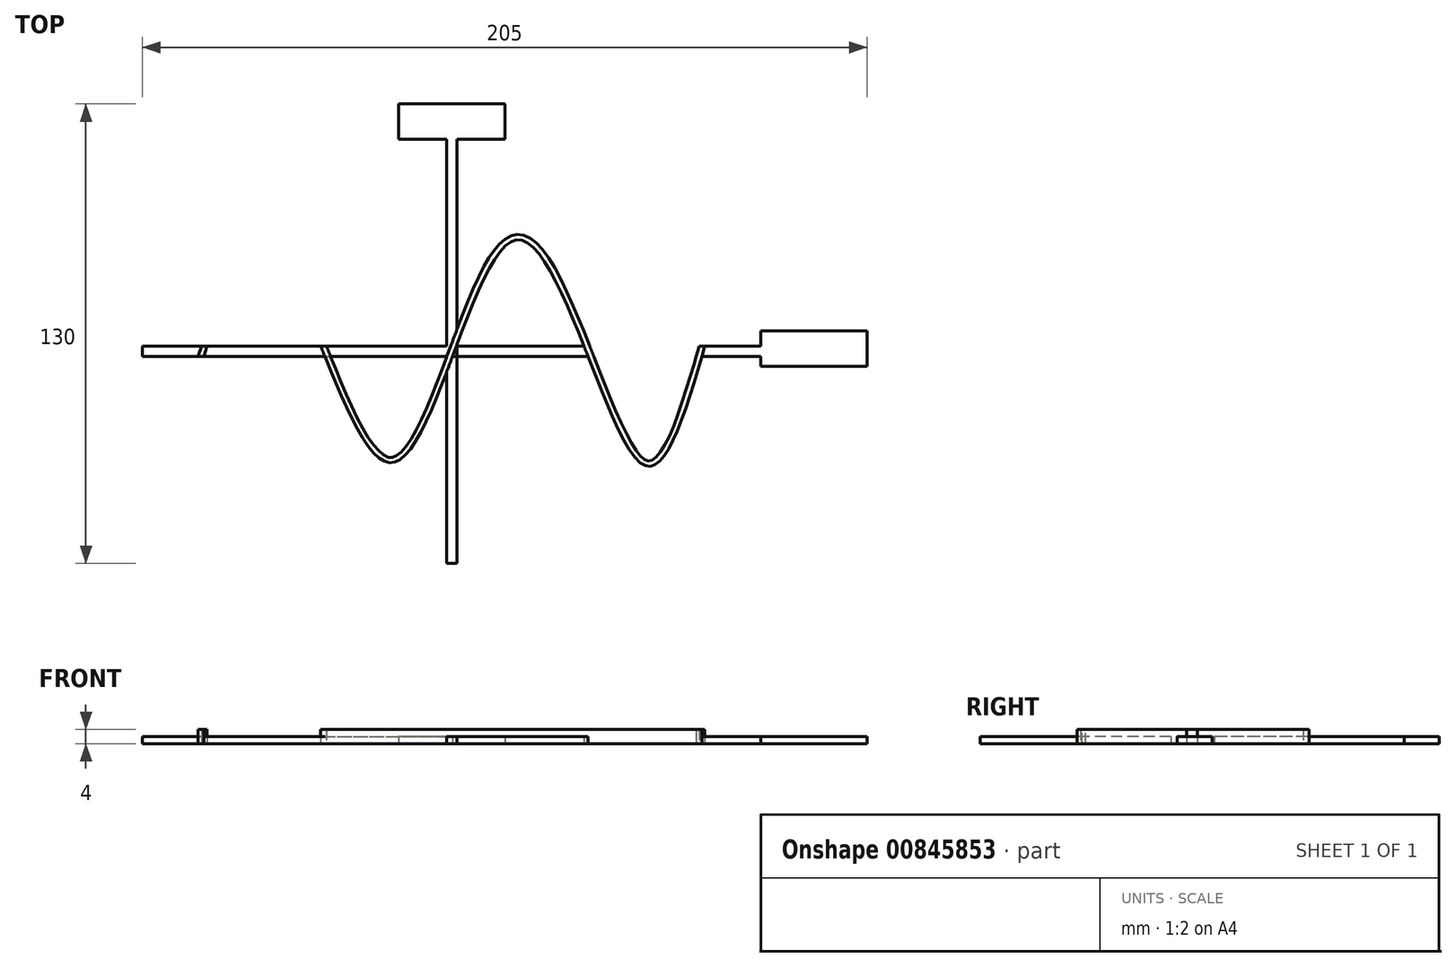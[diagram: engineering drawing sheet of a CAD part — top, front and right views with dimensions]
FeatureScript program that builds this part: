
annotation { "Feature Type Name" : "Feature", "Feature Type Description" : "" }
export const myFeature = defineFeature(function(context is Context, id is Id, definition is map)
    precondition{}
    {
        {
            var Q0;
            Q0=qCreatedBy(makeId("Top.planeOp"),FACE);
            var sketch = newSketch(context, id + "F0", { "sketchPlane" : qUnion([Q0])});
            skLineSegment(sketch, "E0.bottom", {"start": v(-87.5, 1.5) * mm, "end": v(87.5, 1.5) * mm});
            skLineSegment(sketch, "E0.top", {"start": v(-87.5, -1.5) * mm, "end": v(-71.78, -1.5) * mm});
            skLineSegment(sketch, "E0.left", {"start": v(-87.5, 1.5) * mm, "end": v(-87.5, -1.5) * mm});
            skLineSegment(sketch, "E0.right", {"start": v(87.5, 1.5) * mm, "end": v(87.5, -1.5) * mm});
            skLineSegment(sketch, "E1.bottom", {"start": v(-1.5, 60) * mm, "end": v(1.5, 60) * mm});
            skLineSegment(sketch, "E1.top", {"start": v(-1.5, -60) * mm, "end": v(1.5, -60) * mm});
            skLineSegment(sketch, "E1.left", {"start": v(-1.5, 60) * mm, "end": v(-1.5, -60) * mm});
            skLineSegment(sketch, "E1.right", {"start": v(1.5, 60) * mm, "end": v(1.5, -60) * mm});
            skPoint(sketch, "E1.middle", {"position": v(0, 0) * mm});
            skLineSegment(sketch, "E2.bottom", {"start": v(15, 60) * mm, "end": v(-15, 60) * mm});
            skLineSegment(sketch, "E2.top", {"start": v(15, 70) * mm, "end": v(-15, 70) * mm});
            skLineSegment(sketch, "E2.left", {"start": v(15, 60) * mm, "end": v(15, 70) * mm});
            skLineSegment(sketch, "E2.right", {"start": v(-15, 60) * mm, "end": v(-15, 70) * mm});
            skPoint(sketch, "E2.middle", {"position": v(0, 65) * mm});
            skPoint(sketch, "E3", {"position": v(0, 60) * mm});
            skLineSegment(sketch, "E4.bottom", {"start": v(101, -4.26) * mm, "end": v(104, -4.26) * mm});
            skLineSegment(sketch, "E5.bottom", {"start": v(117.5, -4.26) * mm, "end": v(87.5, -4.26) * mm});
            skLineSegment(sketch, "E5.top", {"start": v(117.5, 5.74) * mm, "end": v(87.5, 5.74) * mm});
            skLineSegment(sketch, "E5.left", {"start": v(117.5, -4.26) * mm, "end": v(117.5, 5.74) * mm});
            skLineSegment(sketch, "E5.right", {"start": v(87.5, -4.26) * mm, "end": v(87.5, 5.74) * mm});
            skPoint(sketch, "E5.middle", {"position": v(102.5, 0.74) * mm});
            skPoint(sketch, "E6", {"position": v(102.5, -4.26) * mm});
            skPoint(sketch, "E7", {"position": v(87.5, 0) * mm});
            skPoint(sketch, "E8", {"position": v(0, 1.5) * mm});
            skLineSegment(sketch, "E9", {"start": v(-90, 31.5) * mm, "end": v(86.69, 31.5) * mm, "construction": true});
            skLineSegment(sketch, "E10", {"start": v(-87.09, -31.5) * mm, "end": v(87.56, -31.5) * mm, "construction": true});
            skPoint(sketch, "E11", {"position": v(-70, 31.5) * mm});
            skPoint(sketch, "E12", {"position": v(0, 31.5) * mm});
            skPoint(sketch, "E13", {"position": v(70, 31.5) * mm});
            skPoint(sketch, "E14", {"position": v(-35, -31.5) * mm});
            skPoint(sketch, "E15", {"position": v(35, -31.5) * mm});
            skPoint(sketch, "E16", {"position": v(-70, -31.5) * mm});
            skPoint(sketch, "E17", {"position": v(0.24, -31.5) * mm});
            skPoint(sketch, "E18", {"position": v(70, -31.5) * mm});
            skPoint(sketch, "E19", {"position": v(-35, 31.5) * mm});
            skPoint(sketch, "E20", {"position": v(35, 31.5) * mm});
            skPoint(sketch, "E21", {"position": v(-17.5, -31.5) * mm});
            skPoint(sketch, "E22", {"position": v(17.5, -31.5) * mm});
            skPoint(sketch, "E23", {"position": v(52.5, -31.5) * mm});
            skPoint(sketch, "E24", {"position": v(17.5, 31.5) * mm});
            skPoint(sketch, "E25", {"position": v(52.5, 31.5) * mm});
            skPoint(sketch, "E26", {"position": v(-52.5, 31.5) * mm});
            skPoint(sketch, "E27", {"position": v(-52.5, -31.5) * mm});
            skPoint(sketch, "E28", {"position": v(-17.5, 31.5) * mm});
            skFitSpline(sketch, "E29", {"points": [v(-69.25, 1.5) * mm, v(-51.75, 31.5) * mm, v(-16.75, -31.5) * mm, v(18.25, 31.5) * mm, v(53.25, -31.5) * mm, v(70.75, -1.5) * mm], "startDerivative": vector(100.86, 337.44) * mm, "endDerivative": vector(100.86, 337.44) * mm});
            skFitSpline(sketch, "E30.0", {"points": [v(-70.69, 1.93) * mm, v(-70.16, 3.69) * mm, v(-69.1, 7.2) * mm, v(-67.52, 12.36) * mm, v(-65.9, 17.26) * mm, v(-64.26, 21.78) * mm, v(-62.55, 25.79) * mm, v(-61.07, 28.6) * mm, v(-59.82, 30.5) * mm, v(-58.83, 31.73) * mm, v(-57.76, 32.75) * mm, v(-56.58, 33.53) * mm, v(-55.26, 34.02) * mm, v(-53.82, 34.1) * mm, v(-52.4, 33.72) * mm, v(-51.1, 32.96) * mm, v(-49.89, 31.87) * mm, v(-48.74, 30.5) * mm, v(-47.6, 28.87) * mm, v(-46.1, 26.37) * mm, v(-44.21, 22.67) * mm, v(-41.9, 17.49) * mm, v(-39.54, 11.77) * mm, v(-37.13, 5.7) * mm, v(-34.69, -0.51) * mm, v(-32.22, -6.66) * mm, v(-29.73, -12.53) * mm, v(-27.24, -17.91) * mm, v(-24.76, -22.6) * mm, v(-22.72, -25.73) * mm, v(-21.15, -27.65) * mm, v(-20.02, -28.77) * mm, v(-18.97, -29.54) * mm, v(-18.04, -29.95) * mm, v(-17.38, -30.05) * mm, v(-16.89, -30.01) * mm, v(-16.37, -29.89) * mm, v(-15.63, -29.54) * mm, v(-14.61, -28.75) * mm, v(-13.52, -27.58) * mm, v(-12.01, -25.58) * mm, v(-10.08, -22.31) * mm, v(-7.73, -17.43) * mm, v(-5.37, -11.84) * mm, v(-3.02, -5.78) * mm, v(-0.66, 0.52) * mm, v(1.71, 6.85) * mm, v(4.09, 12.96) * mm, v(6.49, 18.65) * mm, v(8.5, 22.86) * mm, v(10.16, 25.8) * mm, v(11.41, 27.78) * mm, v(12.7, 29.5) * mm, v(14.04, 30.93) * mm, v(15.47, 32.07) * mm, v(16.78, 32.71) * mm, v(17.9, 32.99) * mm, v(19.06, 33.08) * mm, v(20.48, 32.84) * mm, v(22.05, 32.1) * mm, v(23.5, 31.03) * mm, v(24.89, 29.65) * mm, v(26.68, 27.46) * mm, v(28.86, 24.1) * mm, v(31.43, 19.23) * mm, v(33.98, 13.73) * mm, v(36.5, 7.8) * mm, v(38.98, 1.61) * mm, v(41.42, -4.6) * mm, v(43.82, -10.65) * mm, v(46.16, -16.31) * mm, v(48.43, -21.39) * mm, v(50.25, -24.94) * mm, v(51.64, -27.25) * mm, v(52.64, -28.7) * mm, v(53.42, -29.62) * mm, v(54, -30.18) * mm, v(54.53, -30.6) * mm, v(55.1, -30.93) * mm, v(55.65, -31.06) * mm, v(56.13, -31.04) * mm, v(56.68, -30.85) * mm, v(57.35, -30.42) * mm, v(58.1, -29.71) * mm, v(58.88, -28.74) * mm, v(59.96, -27.12) * mm, v(61.33, -24.53) * mm, v(62.96, -20.7) * mm, v(64.57, -16.29) * mm, v(66.16, -11.46) * mm, v(67.74, -6.34) * mm, v(68.79, -2.83) * mm, v(69.31, -1.07) * mm]});
            skFitSpline(sketch, "E31", {"points": [v(-70.69, 1.93) * mm, v(-71.77, -1.5) * mm, v(-71.78, -1.5) * mm], "startDerivative": vector(-1.57, -5.39) * mm, "endDerivative": vector(-0.25, 0.12) * mm});
            skFitSpline(sketch, "E32.trimOffspring", {"points": [v(-70.69, 1.93) * mm, v(-71.77, -1.5) * mm, v(-71.78, -1.5) * mm], "startDerivative": vector(-1.57, -5.39) * mm, "endDerivative": vector(-0.25, 0.12) * mm});
            skLineSegment(sketch, "E33.trimOffspring", {"start": v(-71.77, -1.5) * mm, "end": v(87.5, -1.5) * mm});
            skLineSegment(sketch, "E34", {"start": v(69.18, -1.5) * mm, "end": v(70.01, 1.5) * mm});
            skLineSegment(sketch, "E35", {"start": v(70.75, -1.5) * mm, "end": v(71.57, 1.5) * mm});
            skLineSegment(sketch, "E36", {"start": v(-70.81, 1.5) * mm, "end": v(-71.77, -1.5) * mm});
            skLineSegment(sketch, "E37", {"start": v(-69.25, 1.5) * mm, "end": v(-70.2, -1.5) * mm});
            skSolve(sketch);
        }
        {
            var Q0;
            Q0=makeQuery(id+"F0.imprint","IMPRINT",FACE,{"disambiguationData":[TD([[makeQuery(id+"F0.imprint","IMPRINT",EDGE,{"derivedFrom":sQuery(id+"F0.wireOp",EDGE,"E0.top")}),1.0]])]});
            var Q1;
            {var subQ0=sQuery(id+"F0.wireOp",EDGE,"E30.0");var subQ1=sQuery(id+"F0.wireOp",EDGE,"E0.bottom");var subQ2=makeQuery(id+"F0.imprint","INTERSECT",VERTEX,{"disambiguationData":[OD(0.0)],"derivedFrom":[subQ1,subQ0]});Q1=makeQuery(id+"F0.imprint","IMPRINT",FACE,{"disambiguationData":[TD([[makeQuery(id+"F0.imprint","IMPRINT",EDGE,{"disambiguationData":[TD([[subQ2,-1.0]])],"derivedFrom":subQ1}),-1.0]])]});}
            var Q2;
            {var subQ5=sQuery(id+"F0.wireOp",EDGE,"E1.left");var subQ7=sQuery(id+"F0.wireOp",EDGE,"E0.bottom");var subQ8=makeQuery(id+"F0.imprint","INTERSECT",VERTEX,{"derivedFrom":[subQ7,subQ5]});Q2=makeQuery(id+"F0.imprint","IMPRINT",FACE,{"disambiguationData":[TD([[makeQuery(id+"F0.imprint","IMPRINT",EDGE,{"disambiguationData":[TD([[subQ8,-1.0]])],"derivedFrom":subQ7}),1.0]])]});}
            var Q3;
            {var subQ7=sQuery(id+"F0.wireOp",EDGE,"E1.top");Q3=makeQuery(id+"F0.imprint","IMPRINT",FACE,{"disambiguationData":[TD([[makeQuery(id+"F0.imprint","IMPRINT",EDGE,{"derivedFrom":subQ7}),1.0]])]});}
            var Q4;
            {var subQ0=sQuery(id+"F0.wireOp",EDGE,"E1.right");var subQ1=sQuery(id+"F0.wireOp",EDGE,"E0.bottom");var subQ2=makeQuery(id+"F0.imprint","INTERSECT",VERTEX,{"derivedFrom":[subQ1,subQ0]});Q4=makeQuery(id+"F0.imprint","IMPRINT",FACE,{"disambiguationData":[TD([[makeQuery(id+"F0.imprint","IMPRINT",EDGE,{"disambiguationData":[TD([[subQ2,-1.0]])],"derivedFrom":subQ1}),-1.0]])]});}
            var Q5;
            {var subQ1=sQuery(id+"F0.wireOp",EDGE,"E0.bottom");var subQ6=sQuery(id+"F0.wireOp",EDGE,"E5.right");var subQ7=makeQuery(id+"F0.imprint","INTERSECT",VERTEX,{"derivedFrom":[subQ1,subQ6]});Q5=makeQuery(id+"F0.imprint","IMPRINT",FACE,{"disambiguationData":[TD([[makeQuery(id+"F0.imprint","IMPRINT",EDGE,{"disambiguationData":[TD([[subQ7,1.0]])],"derivedFrom":subQ1}),-1.0]])]});}
            var Q6;
            {var subQ5=sQuery(id+"F0.wireOp",EDGE,"E5.top");Q6=makeQuery(id+"F0.imprint","IMPRINT",FACE,{"disambiguationData":[TD([[makeQuery(id+"F0.imprint","IMPRINT",EDGE,{"derivedFrom":subQ5}),1.0]])]});}
            var Q7;
            Q7=makeQuery(id+"F0.imprint","IMPRINT",FACE,{"disambiguationData":[TD([[makeQuery(id+"F0.imprint","IMPRINT",EDGE,{"derivedFrom":sQuery(id+"F0.wireOp",EDGE,"E2.top")}),1.0]])]});
            var Q8;
            {var subQ0=sQuery(id+"F0.wireOp",EDGE,"E37");Q8=makeQuery(id+"F0.imprint","IMPRINT",FACE,{"disambiguationData":[TD([[makeQuery(id+"F0.imprint","IMPRINT",EDGE,{"derivedFrom":subQ0}),1.0]])]});}
            var Q9;
            {var subQ0=sQuery(id+"F0.wireOp",EDGE,"E34");Q9=makeQuery(id+"F0.imprint","IMPRINT",FACE,{"disambiguationData":[TD([[makeQuery(id+"F0.imprint","IMPRINT",EDGE,{"derivedFrom":subQ0}),1.0]])]});}
            var Q10;
            {var subQ0=sQuery(id+"F0.wireOp",EDGE,"E29");var subQ1=sQuery(id+"F0.wireOp",EDGE,"E0.bottom");var subQ2=makeQuery(id+"F0.imprint","INTERSECT",VERTEX,{"disambiguationData":[OD(1.0)],"derivedFrom":[subQ1,subQ0]});Q10=makeQuery(id+"F0.imprint","IMPRINT",FACE,{"disambiguationData":[TD([[makeQuery(id+"F0.imprint","IMPRINT",EDGE,{"disambiguationData":[TD([[subQ2,-1.0]])],"derivedFrom":subQ1}),-1.0]])]});}
            var Q11;
            {var subQ0=sQuery(id+"F0.wireOp",EDGE,"E1.left");var subQ1=sQuery(id+"F0.wireOp",EDGE,"E0.bottom");var subQ2=makeQuery(id+"F0.imprint","INTERSECT",VERTEX,{"derivedFrom":[subQ1,subQ0]});Q11=makeQuery(id+"F0.imprint","IMPRINT",FACE,{"disambiguationData":[TD([[makeQuery(id+"F0.imprint","IMPRINT",EDGE,{"disambiguationData":[TD([[subQ2,-1.0]])],"derivedFrom":subQ1}),-1.0]])]});}
            extrude(context, id + "F1", {"entities" : qUnion([Q0, Q1, Q2, Q3, Q4, Q5, Q6, Q7, Q8, Q9, Q10, Q11]), "depth" : 2 * mm, "offsetDistance" : 25 * mm});
        }
        {
            var Q0;
            {var subQ2=sQuery(id+"F0.wireOp",EDGE,"E36");Q0=makeQuery(id+"F0.imprint","IMPRINT",FACE,{"disambiguationData":[TD([[makeQuery(id+"F0.imprint","IMPRINT",EDGE,{"derivedFrom":subQ2}),1.0]])]});}
            var Q1;
            {var subQ0=sQuery(id+"F0.wireOp",EDGE,"E31");Q1=makeQuery(id+"F0.imprint","IMPRINT",FACE,{"disambiguationData":[TD([[makeQuery(id+"F0.imprint","IMPRINT",EDGE,{"derivedFrom":subQ0}),1.0]])]});}
            var Q2;
            {var subQ0=sQuery(id+"F0.wireOp",EDGE,"E30.0");var subQ1=sQuery(id+"F0.wireOp",EDGE,"E0.bottom");var subQ2=makeQuery(id+"F0.imprint","INTERSECT",VERTEX,{"disambiguationData":[OD(0.0)],"derivedFrom":[subQ1,subQ0]});Q2=makeQuery(id+"F0.imprint","IMPRINT",FACE,{"disambiguationData":[TD([[makeQuery(id+"F0.imprint","IMPRINT",EDGE,{"disambiguationData":[TD([[subQ2,1.0]])],"derivedFrom":subQ1}),-1.0]])]});}
            var Q3;
            {var subQ0=sQuery(id+"F0.wireOp",EDGE,"E29");var subQ1=sQuery(id+"F0.wireOp",EDGE,"E1.left");var subQ2=makeQuery(id+"F0.imprint","INTERSECT",VERTEX,{"derivedFrom":[subQ1,subQ0]});Q3=makeQuery(id+"F0.imprint","IMPRINT",FACE,{"disambiguationData":[TD([[makeQuery(id+"F0.imprint","IMPRINT",EDGE,{"disambiguationData":[TD([[subQ2,1.0]])],"derivedFrom":subQ1}),-1.0]])]});}
            var Q4;
            {var subQ0=sQuery(id+"F0.wireOp",EDGE,"E29");var subQ1=sQuery(id+"F0.wireOp",EDGE,"E1.left");var subQ2=makeQuery(id+"F0.imprint","INTERSECT",VERTEX,{"derivedFrom":[subQ1,subQ0]});Q4=makeQuery(id+"F0.imprint","IMPRINT",FACE,{"disambiguationData":[TD([[makeQuery(id+"F0.imprint","IMPRINT",EDGE,{"disambiguationData":[TD([[subQ2,1.0]])],"derivedFrom":subQ1}),1.0]])]});}
            var Q5;
            {var subQ0=sQuery(id+"F0.wireOp",EDGE,"E30.0");var subQ1=sQuery(id+"F0.wireOp",EDGE,"E0.bottom");var subQ2=makeQuery(id+"F0.imprint","INTERSECT",VERTEX,{"disambiguationData":[OD(2.0)],"derivedFrom":[subQ1,subQ0]});Q5=makeQuery(id+"F0.imprint","IMPRINT",FACE,{"disambiguationData":[TD([[makeQuery(id+"F0.imprint","IMPRINT",EDGE,{"disambiguationData":[TD([[subQ2,-1.0]])],"derivedFrom":subQ1}),-1.0]])]});}
            var Q6;
            {var subQ0=sQuery(id+"F0.wireOp",EDGE,"E30.0");var subQ1=sQuery(id+"F0.wireOp",EDGE,"E0.bottom");var subQ2=makeQuery(id+"F0.imprint","INTERSECT",VERTEX,{"disambiguationData":[OD(1.0)],"derivedFrom":[subQ1,subQ0]});Q6=makeQuery(id+"F0.imprint","IMPRINT",FACE,{"disambiguationData":[TD([[makeQuery(id+"F0.imprint","IMPRINT",EDGE,{"disambiguationData":[TD([[subQ2,1.0]])],"derivedFrom":subQ1}),1.0]])]});}
            var Q7;
            {var subQ0=sQuery(id+"F0.wireOp",EDGE,"E30.0");var subQ1=sQuery(id+"F0.wireOp",EDGE,"E0.bottom");var subQ2=makeQuery(id+"F0.imprint","INTERSECT",VERTEX,{"disambiguationData":[OD(2.0)],"derivedFrom":[subQ1,subQ0]});Q7=makeQuery(id+"F0.imprint","IMPRINT",FACE,{"disambiguationData":[TD([[makeQuery(id+"F0.imprint","IMPRINT",EDGE,{"disambiguationData":[TD([[subQ2,-1.0]])],"derivedFrom":subQ1}),1.0]])]});}
            var Q8;
            {var subQ0=sQuery(id+"F0.wireOp",EDGE,"E30.0");var subQ1=sQuery(id+"F0.wireOp",EDGE,"E0.bottom");var subQ2=makeQuery(id+"F0.imprint","INTERSECT",VERTEX,{"disambiguationData":[OD(1.0)],"derivedFrom":[subQ1,subQ0]});Q8=makeQuery(id+"F0.imprint","IMPRINT",FACE,{"disambiguationData":[TD([[makeQuery(id+"F0.imprint","IMPRINT",EDGE,{"disambiguationData":[TD([[subQ2,1.0]])],"derivedFrom":subQ1}),-1.0]])]});}
            var Q9;
            {var subQ0=sQuery(id+"F0.wireOp",EDGE,"E33.trimOffspring");var subQ1=sQuery(id+"F0.wireOp",EDGE,"E29");var subQ3=makeQuery(id+"F0.imprint","INTERSECT",VERTEX,{"disambiguationData":[OD(1.0)],"derivedFrom":[subQ1,subQ0]});Q9=makeQuery(id+"F0.imprint","IMPRINT",FACE,{"disambiguationData":[TD([[makeQuery(id+"F0.imprint","IMPRINT",EDGE,{"disambiguationData":[TD([[subQ3,-1.0]])],"derivedFrom":subQ0}),-1.0]])]});}
            var Q10;
            {var subQ0=sQuery(id+"F0.wireOp",EDGE,"E34");Q10=makeQuery(id+"F0.imprint","IMPRINT",FACE,{"disambiguationData":[TD([[makeQuery(id+"F0.imprint","IMPRINT",EDGE,{"derivedFrom":subQ0}),-1.0]])]});}
            extrude(context, id + "F2", {"entities" : qUnion([Q0, Q1, Q2, Q3, Q4, Q5, Q6, Q7, Q8, Q9, Q10]), "depth" : 4 * mm, "offsetDistance" : 25 * mm});
        }
    });
